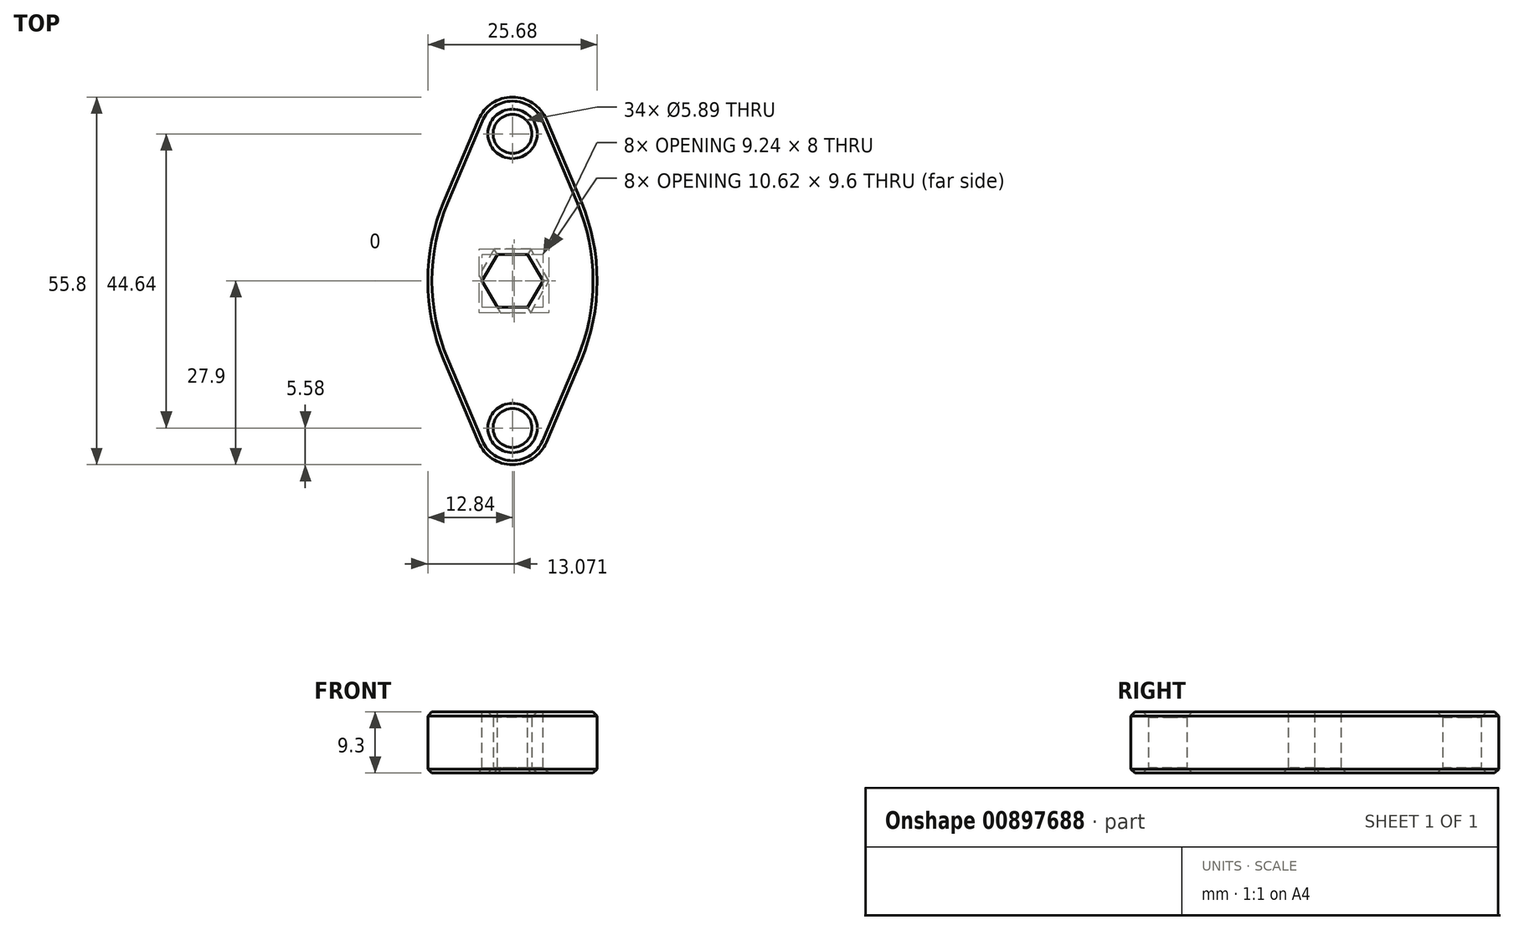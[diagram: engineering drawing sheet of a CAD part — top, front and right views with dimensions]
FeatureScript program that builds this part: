
annotation { "Feature Type Name" : "Feature", "Feature Type Description" : "" }
export const myFeature = defineFeature(function(context is Context, id is Id, definition is map)
    precondition{}
    {
        {
            var Q0;
            Q0=qCreatedBy(makeId("Top.planeOp"),FACE);
            var sketch = newSketch(context, id + "F0", { "sketchPlane" : qUnion([Q0])});
            skLineSegment(sketch, "E0", {"start": v(0, 83.57) * mm, "end": v(0, -89.6) * mm, "construction": true});
            skLineSegment(sketch, "E1", {"start": v(81.05, 0) * mm, "end": v(-79.37, 0) * mm, "construction": true});
            skArc(sketch, "E2", {"start": v(8.29, 39.5) * mm, "mid": v(0, 45) * mm, "end": v(-8.29, 39.5) * mm});
            skLineSegment(sketch, "E3", {"start": v(-26.39, 36) * mm, "end": v(35.06, 36) * mm, "construction": true});
            skArc(sketch, "E4.MirrorCS", {"start": v(8.29, -39.5) * mm, "mid": v(0, -45) * mm, "end": v(-8.29, -39.5) * mm});
            skLineSegment(sketch, "E5", {"start": v(-8.29, 39.5) * mm, "end": v(-25, 0) * mm});
            skLineSegment(sketch, "E6.MirrorCS", {"start": v(8.29, 39.5) * mm, "end": v(25, 0) * mm});
            skPoint(sketch, "E7.orphan", {"position": v(-4.96, 47.37) * mm});
            skPoint(sketch, "E8.orphan", {"position": v(4.96, 47.37) * mm});
            skLineSegment(sketch, "E9.MirrorCS", {"start": v(-8.29, -39.5) * mm, "end": v(-25, 0) * mm});
            skLineSegment(sketch, "E10.MirrorCS", {"start": v(8.29, -39.5) * mm, "end": v(25, 0) * mm});
            skPoint(sketch, "E11.end.orphan", {"position": v(-10, 0) * mm});
            skPoint(sketch, "E11.start.orphan", {"position": v(-9, 36) * mm});
            skPoint(sketch, "E12.end.orphan", {"position": v(10, 0) * mm});
            skPoint(sketch, "E13.orphan", {"position": v(9, 36) * mm});
            skPoint(sketch, "E14.MirrorCS.start.orphan", {"position": v(-9, -36) * mm});
            skPoint(sketch, "E15.orphan", {"position": v(9, -36) * mm});
            skLineSegment(sketch, "E16", {"start": v(-34.58, 46.77) * mm, "end": v(38.96, 46.77) * mm, "construction": true});
            skLineSegment(sketch, "E17.MirrorCS", {"start": v(-34.58, -46.78) * mm, "end": v(38.96, -46.77) * mm, "construction": true});
            skCircle(sketch, "E18", {"center": v(0, 36) * mm, "radius": 11.1 * mm, "construction": true});
            skCircle(sketch, "E19", {"center": v(0, 36) * mm, "radius": 4.75 * mm});
            skCircle(sketch, "E20.MirrorC", {"center": v(0, -36) * mm, "radius": 4.75 * mm});
            skSolve(sketch);
        }
        {
            var Q0;
            Q0=makeQuery(id+"F0.imprint","IMPRINT",FACE,{"disambiguationData":[TD([[makeQuery(id+"F0.imprint","IMPRINT",EDGE,{"derivedFrom":sQuery(id+"F0.wireOp",EDGE,"E2")}),1.0]])]});
            extrude(context, id + "F1", {"entities" : qUnion([Q0]), "endBound" : BoundingType.SYMMETRIC, "depth" : 15 * mm, "offsetDistance" : 25 * mm});
        }
        {
            var Q0;
            Q0=makeQuery(id+"F1.opExtrude","SWEPT_EDGE",EDGE,{"disambiguationData":[OSD([sQuery(id+"F0.wireOp",EDGE,"E5"),sQuery(id+"F0.wireOp",EDGE,"E9.MirrorCS")])]});
            var Q1;
            Q1=makeQuery(id+"F1.opExtrude","SWEPT_EDGE",EDGE,{"disambiguationData":[OSD([sQuery(id+"F0.wireOp",EDGE,"E6.MirrorCS"),sQuery(id+"F0.wireOp",EDGE,"E10.MirrorCS")])]});
            fillet(context, id + "F2", {"entities" : qUnion([Q0, Q1]), "radius" : 50 * mm, "tangentPropagation" : true, "allowEdgeOverflow" : false});
        }
        {
            var Q0;
            Q0=makeQuery(id+"F1.opExtrude","CAP_EDGE",EDGE,{"disambiguationData":[OSD([sQuery(id+"F0.wireOp",EDGE,"E2")])],"isStart":false});
            var Q1;
            Q1=makeQuery(id+"F1.opExtrude","CAP_EDGE",EDGE,{"disambiguationData":[OSD([sQuery(id+"F0.wireOp",EDGE,"E2")])],"isStart":true});
            var Q2;
            Q2=makeQuery(id+"F1.opExtrude","CAP_EDGE",EDGE,{"disambiguationData":[OSD([sQuery(id+"F0.wireOp",EDGE,"E9.MirrorCS")])],"isStart":false});
            var Q3;
            Q3=makeQuery(id+"F1.opExtrude","CAP_EDGE",EDGE,{"disambiguationData":[OSD([sQuery(id+"F0.wireOp",EDGE,"E9.MirrorCS")])],"isStart":true});
            chamfer(context, id + "F3", {"entities" : qUnion([Q0, Q1, Q2, Q3]), "width" : 1 * mm, "tangentPropagation" : true});
        }
        {
            var Q0;
            Q0=makeQuery(id+"F1.opExtrude","SWEPT_BODY",BODY,{"disambiguationData":[OSD([sQuery(id+"F0.wireOp",EDGE,"E2"),sQuery(id+"F0.wireOp",EDGE,"E4.MirrorCS"),sQuery(id+"F0.wireOp",EDGE,"E5"),sQuery(id+"F0.wireOp",EDGE,"E6.MirrorCS"),sQuery(id+"F0.wireOp",EDGE,"E9.MirrorCS"),sQuery(id+"F0.wireOp",EDGE,"E10.MirrorCS"),sQuery(id+"F0.wireOp",EDGE,"E19"),sQuery(id+"F0.wireOp",EDGE,"E20.MirrorC")])]});
            var Q1;
            Q1=qCreatedBy(makeId("Origin.pointOp"),VERTEX);
            transform(context, id + "F4", {"entities" : qUnion([Q0]), "transformType" : TransformType.SCALE_UNIFORMLY, "scale" : .62, "scalePoint" : qUnion([Q1]), "makeCopy" : false});
        }
        {
            var Q0;
            Q0=makeQuery(id+"F1.opExtrude","CAP_FACE",FACE,{"disambiguationData":[OSD([sQuery(id+"F0.wireOp",EDGE,"E2"),sQuery(id+"F0.wireOp",EDGE,"E4.MirrorCS"),sQuery(id+"F0.wireOp",EDGE,"E5"),sQuery(id+"F0.wireOp",EDGE,"E6.MirrorCS"),sQuery(id+"F0.wireOp",EDGE,"E9.MirrorCS"),sQuery(id+"F0.wireOp",EDGE,"E10.MirrorCS"),sQuery(id+"F0.wireOp",EDGE,"E19"),sQuery(id+"F0.wireOp",EDGE,"E20.MirrorC")])],"isStart":false});
            var sketch = newSketch(context, id + "F5", { "sketchPlane" : qUnion([Q0])});
            skLineSegment(sketch, "E21", {"start": v(-6.02, 0) * mm, "end": v(6.38, 0) * mm, "construction": true});
            skLineSegment(sketch, "E22", {"start": v(0, 0) * mm, "end": v(-2.93, 5.07) * mm, "construction": true});
            skLineSegment(sketch, "E23.MirrorCS", {"start": v(0, 0) * mm, "end": v(2.93, 5.07) * mm, "construction": true});
            skLineSegment(sketch, "E24.MirrorCS", {"start": v(0, 0) * mm, "end": v(-2.93, -5.07) * mm, "construction": true});
            skLineSegment(sketch, "E25.MirrorCS", {"start": v(0, 0) * mm, "end": v(2.93, -5.07) * mm, "construction": true});
            skLineSegment(sketch, "E26", {"start": v(-4.62, 0) * mm, "end": v(-2.3, 4) * mm});
            skLineSegment(sketch, "E27", {"start": v(-2.3, 4) * mm, "end": v(2.3, 4) * mm});
            skLineSegment(sketch, "E28", {"start": v(2.3, 4) * mm, "end": v(4.62, 0) * mm});
            skLineSegment(sketch, "E29", {"start": v(4.62, 0) * mm, "end": v(2.3, -4) * mm});
            skLineSegment(sketch, "E30", {"start": v(2.3, -4) * mm, "end": v(-2.3, -4) * mm});
            skLineSegment(sketch, "E31", {"start": v(-2.3, -4) * mm, "end": v(-4.62, 0) * mm});
            skSolve(sketch);
        }
        {
            var Q0;
            Q0=qSketchRegion(id+"F5",true);
            extrude(context, id + "F6", {"entities" : qUnion([Q0]), "operationType" : NewBodyOperationType.REMOVE, "oppositeDirection" : true, "depth" : 25 * mm, "offsetDistance" : 25 * mm});
        }
        {
            var Q0;
            Q0=makeQuery(id+"F1.opExtrude","CAP_EDGE",EDGE,{"disambiguationData":[OSD([sQuery(id+"F0.wireOp",EDGE,"E19")])],"isStart":false});
            var Q1;
            Q1=makeQuery(id+"F1.opExtrude","CAP_EDGE",EDGE,{"disambiguationData":[OSD([sQuery(id+"F0.wireOp",EDGE,"E19")])],"isStart":true});
            var Q2;
            Q2=makeQuery(id+"F1.opExtrude","CAP_EDGE",EDGE,{"disambiguationData":[OSD([sQuery(id+"F0.wireOp",EDGE,"E20.MirrorC")])],"isStart":false});
            var Q3;
            Q3=makeQuery(id+"F1.opExtrude","CAP_EDGE",EDGE,{"disambiguationData":[OSD([sQuery(id+"F0.wireOp",EDGE,"E20.MirrorC")])],"isStart":true});
            var Q4;
            Q4=makeQuery(id+"F6.boolean.opBoolean","COPY",EDGE,{"derivedFrom":makeQuery(id+"F6.opExtrude","CAP_EDGE",EDGE,{"disambiguationData":[OSD([sQuery(id+"F5.wireOp",EDGE,"E30")])],"isStart":true})});
            var Q5;
            Q5=makeQuery(id+"F6.boolean.opBoolean","COPY",EDGE,{"derivedFrom":makeQuery(id+"F6.opExtrude","CAP_EDGE",EDGE,{"disambiguationData":[OSD([sQuery(id+"F5.wireOp",EDGE,"E31")])],"isStart":true})});
            var Q6;
            Q6=makeQuery(id+"F6.boolean.opBoolean","COPY",EDGE,{"derivedFrom":makeQuery(id+"F6.opExtrude","CAP_EDGE",EDGE,{"disambiguationData":[OSD([sQuery(id+"F5.wireOp",EDGE,"E26")])],"isStart":true})});
            var Q7;
            Q7=makeQuery(id+"F6.boolean.opBoolean","COPY",EDGE,{"derivedFrom":makeQuery(id+"F6.opExtrude","CAP_EDGE",EDGE,{"disambiguationData":[OSD([sQuery(id+"F5.wireOp",EDGE,"E27")])],"isStart":true})});
            var Q8;
            Q8=makeQuery(id+"F6.boolean.opBoolean","COPY",EDGE,{"derivedFrom":makeQuery(id+"F6.opExtrude","CAP_EDGE",EDGE,{"disambiguationData":[OSD([sQuery(id+"F5.wireOp",EDGE,"E28")])],"isStart":true})});
            var Q9;
            Q9=makeQuery(id+"F6.boolean.opBoolean","COPY",EDGE,{"derivedFrom":makeQuery(id+"F6.opExtrude","CAP_EDGE",EDGE,{"disambiguationData":[OSD([sQuery(id+"F5.wireOp",EDGE,"E29")])],"isStart":true})});
            var Q10;
            Q10=makeQuery(id+"F6.boolean.opBoolean","INTERSECT",EDGE,{"derivedFrom":[makeQuery(id+"F1.opExtrude","CAP_FACE",FACE,{"disambiguationData":[OSD([sQuery(id+"F0.wireOp",EDGE,"E2"),sQuery(id+"F0.wireOp",EDGE,"E4.MirrorCS"),sQuery(id+"F0.wireOp",EDGE,"E5"),sQuery(id+"F0.wireOp",EDGE,"E6.MirrorCS"),sQuery(id+"F0.wireOp",EDGE,"E9.MirrorCS"),sQuery(id+"F0.wireOp",EDGE,"E10.MirrorCS"),sQuery(id+"F0.wireOp",EDGE,"E19"),sQuery(id+"F0.wireOp",EDGE,"E20.MirrorC")])],"isStart":true}),makeQuery(id+"F6.opExtrude","SWEPT_FACE",FACE,{"disambiguationData":[OSD([sQuery(id+"F5.wireOp",EDGE,"E30")])]})]});
            var Q11;
            Q11=makeQuery(id+"F6.boolean.opBoolean","INTERSECT",EDGE,{"derivedFrom":[makeQuery(id+"F1.opExtrude","CAP_FACE",FACE,{"disambiguationData":[OSD([sQuery(id+"F0.wireOp",EDGE,"E2"),sQuery(id+"F0.wireOp",EDGE,"E4.MirrorCS"),sQuery(id+"F0.wireOp",EDGE,"E5"),sQuery(id+"F0.wireOp",EDGE,"E6.MirrorCS"),sQuery(id+"F0.wireOp",EDGE,"E9.MirrorCS"),sQuery(id+"F0.wireOp",EDGE,"E10.MirrorCS"),sQuery(id+"F0.wireOp",EDGE,"E19"),sQuery(id+"F0.wireOp",EDGE,"E20.MirrorC")])],"isStart":true}),makeQuery(id+"F6.opExtrude","SWEPT_FACE",FACE,{"disambiguationData":[OSD([sQuery(id+"F5.wireOp",EDGE,"E29")])]})]});
            var Q12;
            Q12=makeQuery(id+"F6.boolean.opBoolean","INTERSECT",EDGE,{"derivedFrom":[makeQuery(id+"F1.opExtrude","CAP_FACE",FACE,{"disambiguationData":[OSD([sQuery(id+"F0.wireOp",EDGE,"E2"),sQuery(id+"F0.wireOp",EDGE,"E4.MirrorCS"),sQuery(id+"F0.wireOp",EDGE,"E5"),sQuery(id+"F0.wireOp",EDGE,"E6.MirrorCS"),sQuery(id+"F0.wireOp",EDGE,"E9.MirrorCS"),sQuery(id+"F0.wireOp",EDGE,"E10.MirrorCS"),sQuery(id+"F0.wireOp",EDGE,"E19"),sQuery(id+"F0.wireOp",EDGE,"E20.MirrorC")])],"isStart":true}),makeQuery(id+"F6.opExtrude","SWEPT_FACE",FACE,{"disambiguationData":[OSD([sQuery(id+"F5.wireOp",EDGE,"E28")])]})]});
            var Q13;
            Q13=makeQuery(id+"F6.boolean.opBoolean","INTERSECT",EDGE,{"derivedFrom":[makeQuery(id+"F1.opExtrude","CAP_FACE",FACE,{"disambiguationData":[OSD([sQuery(id+"F0.wireOp",EDGE,"E2"),sQuery(id+"F0.wireOp",EDGE,"E4.MirrorCS"),sQuery(id+"F0.wireOp",EDGE,"E5"),sQuery(id+"F0.wireOp",EDGE,"E6.MirrorCS"),sQuery(id+"F0.wireOp",EDGE,"E9.MirrorCS"),sQuery(id+"F0.wireOp",EDGE,"E10.MirrorCS"),sQuery(id+"F0.wireOp",EDGE,"E19"),sQuery(id+"F0.wireOp",EDGE,"E20.MirrorC")])],"isStart":true}),makeQuery(id+"F6.opExtrude","SWEPT_FACE",FACE,{"disambiguationData":[OSD([sQuery(id+"F5.wireOp",EDGE,"E27")])]})]});
            var Q14;
            Q14=makeQuery(id+"F6.boolean.opBoolean","INTERSECT",EDGE,{"derivedFrom":[makeQuery(id+"F1.opExtrude","CAP_FACE",FACE,{"disambiguationData":[OSD([sQuery(id+"F0.wireOp",EDGE,"E2"),sQuery(id+"F0.wireOp",EDGE,"E4.MirrorCS"),sQuery(id+"F0.wireOp",EDGE,"E5"),sQuery(id+"F0.wireOp",EDGE,"E6.MirrorCS"),sQuery(id+"F0.wireOp",EDGE,"E9.MirrorCS"),sQuery(id+"F0.wireOp",EDGE,"E10.MirrorCS"),sQuery(id+"F0.wireOp",EDGE,"E19"),sQuery(id+"F0.wireOp",EDGE,"E20.MirrorC")])],"isStart":true}),makeQuery(id+"F6.opExtrude","SWEPT_FACE",FACE,{"disambiguationData":[OSD([sQuery(id+"F5.wireOp",EDGE,"E26")])]})]});
            chamfer(context, id + "F7", {"entities" : qUnion([Q0, Q1, Q2, Q3, Q4, Q5, Q6, Q7, Q8, Q9, Q10, Q11, Q12, Q13, Q14]), "width" : .8 * mm, "tangentPropagation" : true});
        }
    });
